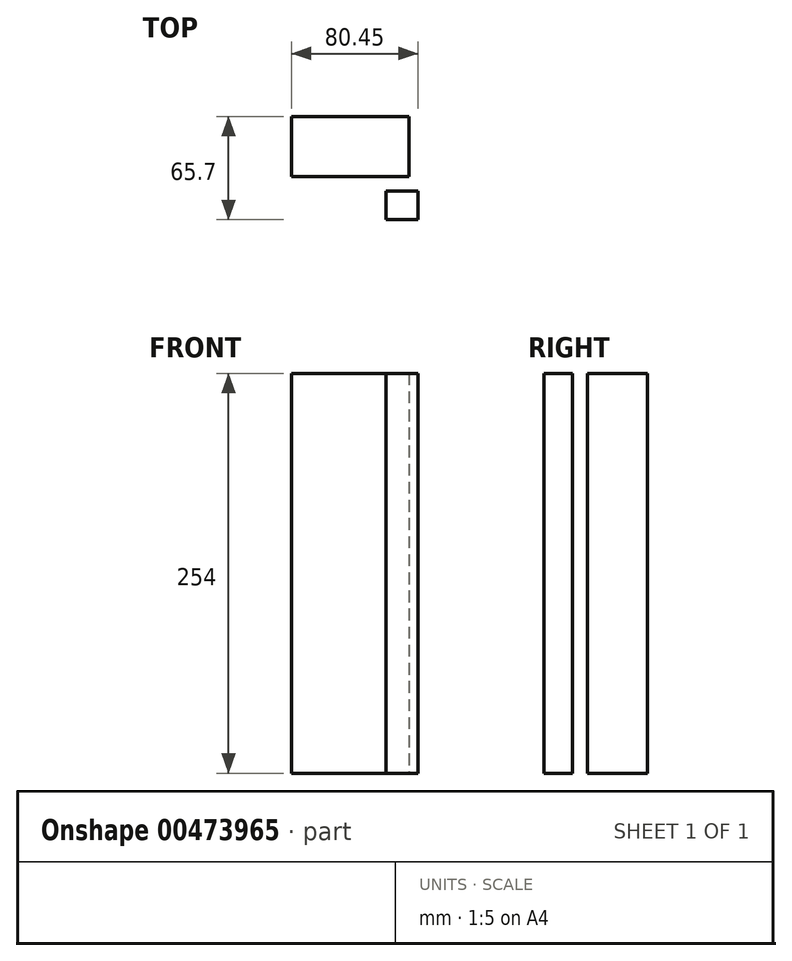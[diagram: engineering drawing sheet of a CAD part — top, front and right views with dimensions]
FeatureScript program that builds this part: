
annotation { "Feature Type Name" : "Feature", "Feature Type Description" : "" }
export const myFeature = defineFeature(function(context is Context, id is Id, definition is map)
    precondition{}
    {
        {
            var Q0;
            Q0=qCreatedBy(makeId("Top.planeOp"),FACE);
            var sketch = newSketch(context, id + "F0", { "sketchPlane" : qUnion([Q0])});
            skLineSegment(sketch, "E0.bottom", {"start": v(-37.38, 0) * mm, "end": v(37.38, 0) * mm});
            skLineSegment(sketch, "E0.top", {"start": v(-37.38, 38.26) * mm, "end": v(37.38, 38.26) * mm});
            skLineSegment(sketch, "E0.left", {"start": v(-37.38, 0) * mm, "end": v(-37.38, 38.26) * mm});
            skLineSegment(sketch, "E0.right", {"start": v(37.38, 0) * mm, "end": v(37.38, 38.26) * mm});
            skPoint(sketch, "E0.middle", {"position": v(0, 19.13) * mm});
            skLineSegment(sketch, "E1.bottom", {"start": v(22.52, -9.3) * mm, "end": v(43.07, -9.3) * mm});
            skLineSegment(sketch, "E1.top", {"start": v(22.52, -27.44) * mm, "end": v(43.07, -27.44) * mm});
            skLineSegment(sketch, "E1.left", {"start": v(22.52, -9.3) * mm, "end": v(22.52, -27.44) * mm});
            skLineSegment(sketch, "E1.right", {"start": v(43.07, -9.3) * mm, "end": v(43.07, -27.44) * mm});
            skSolve(sketch);
        }
        {
            var Q0;
            Q0 = qSketchRegion(id + "F0", true);
            extrude(context, id + "F1", {"entities" : qUnion([Q0]), "depth" : 254 * mm, "offsetDistance" : 25.4 * mm});
        }
        {
            var Q0;
            Q0=qCreatedBy(makeId("Top.planeOp"),FACE);
            cPlane(context, id + "F2", {"entities" : qUnion([Q0]), "cplaneType" : CPlaneType.OFFSET, "offset" : 101.6 * mm, "width" : 152.4 * mm, "height" : 152.4 * mm});
        }
    });
